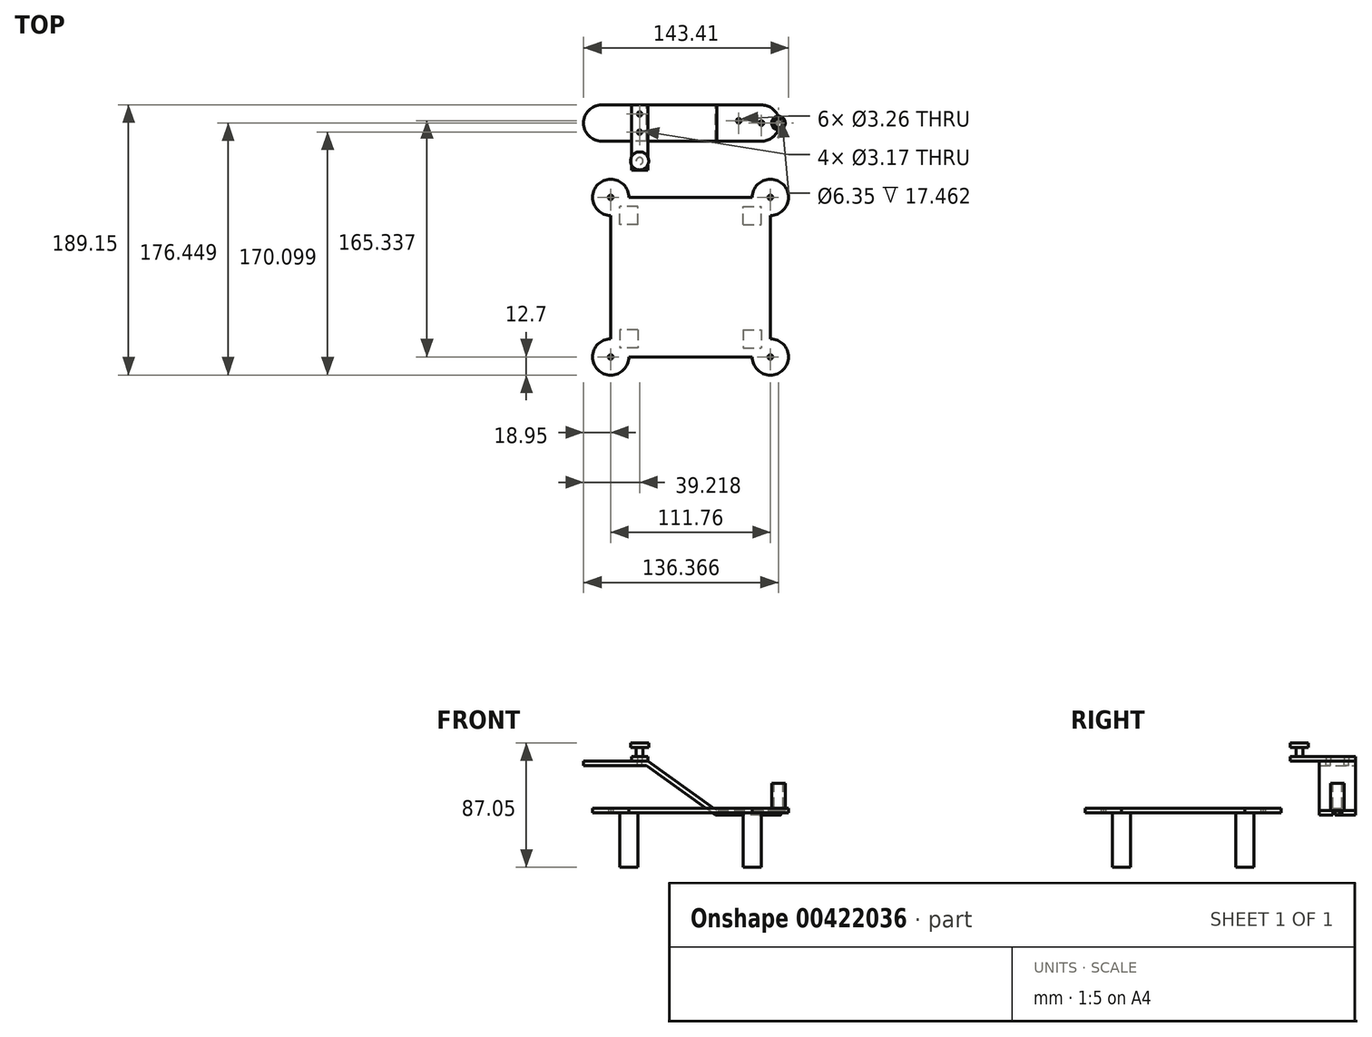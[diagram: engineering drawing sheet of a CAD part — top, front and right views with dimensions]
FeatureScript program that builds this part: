
annotation { "Feature Type Name" : "Feature", "Feature Type Description" : "" }
export const myFeature = defineFeature(function(context is Context, id is Id, definition is map)
    precondition{}
    {
        {
            var Q0;
            Q0=qCreatedBy(makeId("Top.planeOp"),FACE);
            var sketch = newSketch(context, id + "F0", { "sketchPlane" : qUnion([Q0])});
            skLineSegment(sketch, "E0.bottom", {"start": v(-43.18, 55.88) * mm, "end": v(43.18, 55.88) * mm});
            skLineSegment(sketch, "E0.top", {"start": v(-43.18, -55.88) * mm, "end": v(43.18, -55.88) * mm});
            skLineSegment(sketch, "E0.left", {"start": v(-55.88, 43.18) * mm, "end": v(-55.88, -43.18) * mm});
            skLineSegment(sketch, "E0.right", {"start": v(55.88, 43.18) * mm, "end": v(55.88, -43.18) * mm});
            skPoint(sketch, "E0.middle", {"position": v(0, 0) * mm});
            skArc(sketch, "E1", {"start": v(-43.18, 55.88) * mm, "mid": v(-64.86, 64.86) * mm, "end": v(-55.88, 43.18) * mm});
            skLineSegment(sketch, "E2", {"start": v(0, 0) * mm, "end": v(-55.88, 55.88) * mm, "construction": true});
            skArc(sketch, "E3.1.0", {"start": v(-55.88, -43.18) * mm, "mid": v(-64.86, -64.86) * mm, "end": v(-43.18, -55.88) * mm});
            skArc(sketch, "E3.2.0", {"start": v(43.18, -55.88) * mm, "mid": v(64.86, -64.86) * mm, "end": v(55.88, -43.18) * mm});
            skArc(sketch, "E3.3.0", {"start": v(55.88, 43.18) * mm, "mid": v(64.86, 64.86) * mm, "end": v(43.18, 55.88) * mm});
            skLineSegment(sketch, "E4.bottom", {"start": v(31.75, 31.75) * mm, "end": v(-31.75, 31.75) * mm, "construction": true});
            skLineSegment(sketch, "E4.top", {"start": v(31.75, -31.75) * mm, "end": v(-31.75, -31.75) * mm, "construction": true});
            skLineSegment(sketch, "E4.left", {"start": v(31.75, 31.75) * mm, "end": v(31.75, -31.75) * mm, "construction": true});
            skLineSegment(sketch, "E4.right", {"start": v(-31.75, 31.75) * mm, "end": v(-31.75, -31.75) * mm, "construction": true});
            skLineSegment(sketch, "E5.bottom", {"start": v(-43.18, 55.88) * mm, "end": v(39.63, 55.88) * mm});
            skLineSegment(sketch, "E5.top", {"start": v(-43.18, 43.18) * mm, "end": v(39.63, 43.18) * mm});
            skLineSegment(sketch, "E5.left", {"start": v(-43.18, 55.88) * mm, "end": v(-43.18, 43.18) * mm});
            skLineSegment(sketch, "E5.right", {"start": v(39.63, 55.88) * mm, "end": v(39.63, 43.18) * mm});
            skLineSegment(sketch, "E6", {"start": v(14.97, 68.58) * mm, "end": v(-33.08, 68.58) * mm, "construction": true});
            skLineSegment(sketch, "E7", {"start": v(0, 29.37) * mm, "end": v(-29.37, 29.37) * mm, "construction": true});
            skLineSegment(sketch, "E8", {"start": v(-29.37, -8.95) * mm, "end": v(-29.37, 29.37) * mm, "construction": true});
            skSolve(sketch);
        }
        {
            var Q0;
            Q0=qCreatedBy(makeId("Top.planeOp"),FACE);
            var sketch = newSketch(context, id + "F1", { "sketchPlane" : qUnion([Q0])});
            skArc(sketch, "E9", {"start": v(-62.13, 120.57) * mm, "mid": v(-74.83, 107.87) * mm, "end": v(-62.13, 95.17) * mm});
            skLineSegment(sketch, "E10.bottom", {"start": v(-62.13, 95.17) * mm, "end": v(-62.13, 120.57) * mm, "construction": true});
            skLineSegment(sketch, "E10.top", {"start": v(49.63, 95.17) * mm, "end": v(49.63, 120.57) * mm, "construction": true});
            skLineSegment(sketch, "E10.left", {"start": v(-62.13, 95.17) * mm, "end": v(49.63, 95.17) * mm});
            skLineSegment(sketch, "E10.right", {"start": v(-62.13, 120.57) * mm, "end": v(49.63, 120.57) * mm});
            skPoint(sketch, "E10.middle", {"position": v(-6.25, 107.87) * mm});
            skArc(sketch, "E11", {"start": v(49.63, 95.17) * mm, "mid": v(62.33, 107.87) * mm, "end": v(49.63, 120.57) * mm});
            skArc(sketch, "E12", {"start": v(-62.13, 95.17) * mm, "mid": v(-49.43, 107.87) * mm, "end": v(-62.13, 120.57) * mm, "construction": true});
            skCircle(sketch, "E13", {"center": v(49.63, 107.87) * mm, "radius": 12.7 * mm, "construction": true});
            skLineSegment(sketch, "E14", {"start": v(49.63, 107.87) * mm, "end": v(-62.13, 107.87) * mm, "construction": true});
            skPoint(sketch, "E15", {"position": v(36.93, 107.87) * mm});
            skPoint(sketch, "E16", {"position": v(-49.43, 107.87) * mm});
            skSolve(sketch);
        }
        {
            var Q0;
            Q0 = qSketchRegion(id + "F0", true);
            extrude(context, id + "F2", {"entities" : qUnion([Q0]), "depth" : 3.17 * mm});
        }
        {
            var Q0;
            Q0=sQuery(id+"F0.wireOp",VERTEX,"E2.end");
            var Q1;
            Q1=sQuery(id+"F0.wireOp",VERTEX,"E3.3.0.center");
            var Q2;
            Q2=sQuery(id+"F0.wireOp",VERTEX,"E3.1.0.center");
            var Q3;
            Q3=sQuery(id+"F0.wireOp",VERTEX,"E3.2.0.center");
            var Q4;
            Q4=makeQuery(id+"F2.opExtrude","SWEPT_BODY",BODY,{"disambiguationData":[OSD([sQuery(id+"F0.wireOp",EDGE,"E0.bottom"),sQuery(id+"F0.wireOp",EDGE,"E0.top"),sQuery(id+"F0.wireOp",EDGE,"E0.left"),sQuery(id+"F0.wireOp",EDGE,"E0.right"),sQuery(id+"F0.wireOp",EDGE,"E1"),sQuery(id+"F0.wireOp",EDGE,"E3.1.0"),sQuery(id+"F0.wireOp",EDGE,"E3.2.0"),sQuery(id+"F0.wireOp",EDGE,"E3.3.0")])]});
            hole(context, id + "F3", {"style" : HoleStyle.SIMPLE, "endStyle" : HoleEndStyle.THROUGH, "oppositeDirection" : true, "standardTappedOrClearance" : lookupTablePath({ "standard" : "ANSI", "fit" : "Normal (ASME)", "size" : "#4", "type" : "Clearance" }), "standardBlindInLast" : lookupTablePath({ "fit" : "Free", "standard" : "ANSI", "size" : "#4", "type" : "Clearance" }), "holeDiameter" : 3.26 * mm, "isTappedThrough" : true, "tappedDepth" : 12.7 * mm, "tapClearance" : 3, "locations" : qUnion([Q0, Q1, Q2, Q3]), "scope" : qUnion([Q4])});
        }
        {
            var Q0;
            Q0=sQuery(id+"F1.wireOp",EDGE,"E14");
            cPlane(context, id + "F4", {"entities" : qUnion([Q0]), "cplaneType" : CPlaneType.LINE_ANGLE, "offset" : 25.4 * mm, "angle" : 0 * degree, "width" : 152.4 * mm, "height" : 152.4 * mm});
        }
        {
            var Q0;
            Q0=qCreatedBy(id+"F4.planeOp",FACE);
            var sketch = newSketch(context, id + "F5", { "sketchPlane" : qUnion([Q0])});
            skLineSegment(sketch, "E17", {"start": v(49.63, 0) * mm, "end": v(17.88, 0) * mm});
            skLineSegment(sketch, "E18", {"start": v(17.88, 0) * mm, "end": v(-30.38, 34.66) * mm});
            skLineSegment(sketch, "E19", {"start": v(-30.38, 34.66) * mm, "end": v(-62.13, 34.66) * mm});
            skLineSegment(sketch, "E20", {"start": v(-30.38, 34.66) * mm, "end": v(-30.38, 0.01) * mm, "construction": true});
            skLineSegment(sketch, "E21", {"start": v(-62.13, 34.66) * mm, "end": v(-62.13, 0) * mm, "construction": true});
            skSolve(sketch);
        }
        {
            var Q0;
            Q0=sQuery(id+"F1.wireOp",EDGE,"E10.top");
            cPlane(context, id + "F6", {"entities" : qUnion([Q0]), "cplaneType" : CPlaneType.LINE_ANGLE, "offset" : 25.4 * mm, "angle" : 90 * degree, "width" : 152.4 * mm, "height" : 152.4 * mm});
        }
        {
            var Q0;
            Q0=qCreatedBy(id+"F6.planeOp",FACE);
            var sketch = newSketch(context, id + "F7", { "sketchPlane" : qUnion([Q0])});
            skLineSegment(sketch, "E22.bottom", {"start": v(95.17, -1.59) * mm, "end": v(120.57, -1.59) * mm});
            skLineSegment(sketch, "E22.top", {"start": v(95.17, 1.59) * mm, "end": v(120.57, 1.59) * mm});
            skLineSegment(sketch, "E22.left", {"start": v(95.17, -1.59) * mm, "end": v(95.17, 1.59) * mm});
            skLineSegment(sketch, "E22.right", {"start": v(120.57, -1.59) * mm, "end": v(120.57, 1.59) * mm});
            skPoint(sketch, "E23", {"position": v(120.57, 0) * mm});
            skSolve(sketch);
        }
        {
            var Q0;
            Q0 = qSketchRegion(id + "F7", true);
            var Q1;
            Q1 = qConstructionFilter(qBodyType(qCreatedBy(id + "F5" ,EDGE), BodyType.WIRE), ConstructionObject.NO);
            sweep(context, id + "F8", {"profiles" : qUnion([Q0]), "path" : qUnion([Q1])});
        }
        {
            var Q0;
            Q0=makeQuery(id+"F8.opSweep","CAP_FACE",FACE,{"disambiguationData":[OSD([sQuery(id+"F5.wireOp",VERTEX,"E17.start"),sQuery(id+"F7.wireOp",EDGE,"E22.bottom"),sQuery(id+"F7.wireOp",EDGE,"E22.top"),sQuery(id+"F7.wireOp",EDGE,"E22.left"),sQuery(id+"F7.wireOp",EDGE,"E22.right")])],"isStart":true});
            var sketch = newSketch(context, id + "F9", { "sketchPlane" : qUnion([Q0])});
            skLineSegment(sketch, "E24", {"start": v(107.87, 1.59) * mm, "end": v(107.87, -1.59) * mm, "construction": true});
            skLineSegment(sketch, "E25.bottom", {"start": v(107.87, 1.59) * mm, "end": v(120.57, 1.59) * mm});
            skLineSegment(sketch, "E25.top", {"start": v(107.87, -1.59) * mm, "end": v(120.57, -1.59) * mm});
            skLineSegment(sketch, "E25.left", {"start": v(107.87, 1.59) * mm, "end": v(107.87, -1.59) * mm});
            skLineSegment(sketch, "E25.right", {"start": v(120.57, 1.59) * mm, "end": v(120.57, -1.59) * mm});
            skSolve(sketch);
        }
        {
            var Q0;
            Q0 = qSketchRegion(id + "F9", true);
            var Q1;
            Q1=sQuery(id+"F9.wireOp",EDGE,"E25.left");
            revolve(context, id + "F10", {"operationType" : NewBodyOperationType.ADD, "entities" : qUnion([Q0]), "axis" : qUnion([Q1]), "revolveType" : RevolveType.FULL});
        }
        {
            var Q0;
            Q0=makeQuery(id+"F8.opSweep","CAP_FACE",FACE,{"disambiguationData":[OSD([sQuery(id+"F5.wireOp",VERTEX,"E19.end"),sQuery(id+"F7.wireOp",EDGE,"E22.bottom"),sQuery(id+"F7.wireOp",EDGE,"E22.top"),sQuery(id+"F7.wireOp",EDGE,"E22.left"),sQuery(id+"F7.wireOp",EDGE,"E22.right")])],"isStart":false});
            var sketch = newSketch(context, id + "F11", { "sketchPlane" : qUnion([Q0])});
            skLineSegment(sketch, "E26", {"start": v(-107.87, 36.25) * mm, "end": v(-107.87, 33.07) * mm, "construction": true});
            skLineSegment(sketch, "E27.bottom", {"start": v(-107.87, 33.07) * mm, "end": v(-95.17, 33.07) * mm});
            skLineSegment(sketch, "E27.top", {"start": v(-107.87, 36.25) * mm, "end": v(-95.17, 36.25) * mm});
            skLineSegment(sketch, "E27.left", {"start": v(-107.87, 33.07) * mm, "end": v(-107.87, 36.25) * mm});
            skLineSegment(sketch, "E27.right", {"start": v(-95.17, 33.07) * mm, "end": v(-95.17, 36.25) * mm});
            skSolve(sketch);
        }
        {
            var Q0;
            Q0 = qSketchRegion(id + "F11", true);
            var Q1;
            Q1=sQuery(id+"F11.wireOp",EDGE,"E27.left");
            revolve(context, id + "F12", {"operationType" : NewBodyOperationType.ADD, "entities" : qUnion([Q0]), "axis" : qUnion([Q1]), "revolveType" : RevolveType.FULL});
        }
        {
            var Q0;
            Q0=makeQuery(id+"F10.boolean.opBoolean","MERGE",FACE,{"derivedFrom":[makeQuery(id+"F8.opSweep","SWEPT_FACE",FACE,{"disambiguationData":[OSD([sQuery(id+"F5.wireOp",EDGE,"E17"),sQuery(id+"F7.wireOp",EDGE,"E22.top")])]}),makeQuery(id+"F10.opRevolve","SWEPT_FACE",FACE,{"disambiguationData":[OSD([sQuery(id+"F9.wireOp",EDGE,"E25.bottom")])]})]});
            var sketch = newSketch(context, id + "F13", { "sketchPlane" : qUnion([Q0])});
            skPoint(sketch, "E28", {"position": v(49.63, 107.87) * mm});
            skSolve(sketch);
        }
        {
            var Q0;
            Q0=sQuery(id+"F13.wireOp",VERTEX,"E28");
            var Q1;
            Q1=makeQuery(id+"F8.opSweep","SWEPT_BODY",BODY,{"disambiguationData":[OSD([sQuery(id+"F5.wireOp",EDGE,"E19"),sQuery(id+"F7.wireOp",EDGE,"E22.bottom"),sQuery(id+"F7.wireOp",EDGE,"E22.top"),sQuery(id+"F7.wireOp",EDGE,"E22.left"),sQuery(id+"F7.wireOp",EDGE,"E22.right")])]});
            hole(context, id + "F14", {"style" : HoleStyle.SIMPLE, "endStyle" : HoleEndStyle.THROUGH, "standardTappedOrClearance" : lookupTablePath({ "standard" : "ANSI", "fit" : "Normal (ASME)", "size" : "#4", "type" : "Clearance" }), "standardBlindInLast" : lookupTablePath({ "fit" : "Free", "standard" : "ANSI", "size" : "#4", "type" : "Clearance" }), "holeDiameter" : 3.26 * mm, "isTappedThrough" : true, "tappedDepth" : 12.7 * mm, "tapClearance" : 3, "locations" : qUnion([Q0]), "scope" : qUnion([Q1])});
        }
        {
            var Q0;
            Q0=makeQuery(id+"F10.boolean.opBoolean","MERGE",FACE,{"derivedFrom":[makeQuery(id+"F8.opSweep","SWEPT_FACE",FACE,{"disambiguationData":[OSD([sQuery(id+"F5.wireOp",EDGE,"E17"),sQuery(id+"F7.wireOp",EDGE,"E22.top")])]}),makeQuery(id+"F10.opRevolve","SWEPT_FACE",FACE,{"disambiguationData":[OSD([sQuery(id+"F9.wireOp",EDGE,"E25.bottom")])]})]});
            var sketch = newSketch(context, id + "F15", { "sketchPlane" : qUnion([Q0])});
            skPoint(sketch, "E29", {"position": v(33.76, 109.46) * mm});
            skSolve(sketch);
        }
        {
            var Q0;
            Q0=sQuery(id+"F15.wireOp",VERTEX,"E29");
            var Q1;
            Q1=makeQuery(id+"F8.opSweep","SWEPT_BODY",BODY,{"disambiguationData":[OSD([sQuery(id+"F5.wireOp",EDGE,"E19"),sQuery(id+"F7.wireOp",EDGE,"E22.bottom"),sQuery(id+"F7.wireOp",EDGE,"E22.top"),sQuery(id+"F7.wireOp",EDGE,"E22.left"),sQuery(id+"F7.wireOp",EDGE,"E22.right")])]});
            hole(context, id + "F16", {"style" : HoleStyle.SIMPLE, "endStyle" : HoleEndStyle.THROUGH, "standardTappedOrClearance" : lookupTablePath({ "standard" : "ANSI", "fit" : "Normal (ASME)", "size" : "#4", "type" : "Clearance" }), "standardBlindInLast" : lookupTablePath({ "fit" : "Free", "standard" : "ANSI", "size" : "#4", "type" : "Clearance" }), "holeDiameter" : 3.26 * mm, "isTappedThrough" : true, "tappedDepth" : 12.7 * mm, "tapClearance" : 3, "locations" : qUnion([Q0]), "scope" : qUnion([Q1])});
        }
        {
            var Q0;
            Q0=makeQuery(id+"F10.boolean.opBoolean","MERGE",FACE,{"derivedFrom":[makeQuery(id+"F8.opSweep","SWEPT_FACE",FACE,{"disambiguationData":[OSD([sQuery(id+"F5.wireOp",EDGE,"E17"),sQuery(id+"F7.wireOp",EDGE,"E22.top")])]}),makeQuery(id+"F10.opRevolve","SWEPT_FACE",FACE,{"disambiguationData":[OSD([sQuery(id+"F9.wireOp",EDGE,"E25.bottom")])]})]});
            var sketch = newSketch(context, id + "F17", { "sketchPlane" : qUnion([Q0])});
            skPoint(sketch, "E30", {"position": v(62.33, 107.87) * mm});
            skCircle(sketch, "E31", {"center": v(62.33, 107.87) * mm, "radius": 1.59 * mm, "construction": true});
            skCircle(sketch, "E32", {"center": v(62.33, 107.87) * mm, "radius": 3.18 * mm, "construction": true});
            skLineSegment(sketch, "E33.bottom", {"start": v(65.5, 111.04) * mm, "end": v(59.16, 111.04) * mm});
            skLineSegment(sketch, "E33.top", {"start": v(65.5, 104.7) * mm, "end": v(59.16, 104.7) * mm});
            skLineSegment(sketch, "E33.left", {"start": v(65.5, 111.04) * mm, "end": v(65.5, 104.7) * mm});
            skLineSegment(sketch, "E33.right", {"start": v(59.16, 111.04) * mm, "end": v(59.16, 104.7) * mm});
            skSolve(sketch);
        }
        {
            var Q0;
            Q0 = qSketchRegion(id + "F17", true);
            extrude(context, id + "F18", {"entities" : qUnion([Q0]), "operationType" : NewBodyOperationType.REMOVE, "endBound" : BoundingType.THROUGH_ALL, "oppositeDirection" : true, "depth" : 25.4 * mm});
        }
        {
            var Q0;
            Q0=makeQuery(id+"F10.boolean.opBoolean","MERGE",FACE,{"derivedFrom":[makeQuery(id+"F8.opSweep","SWEPT_FACE",FACE,{"disambiguationData":[OSD([sQuery(id+"F5.wireOp",EDGE,"E17"),sQuery(id+"F7.wireOp",EDGE,"E22.top")])]}),makeQuery(id+"F10.opRevolve","SWEPT_FACE",FACE,{"disambiguationData":[OSD([sQuery(id+"F9.wireOp",EDGE,"E25.bottom")])]})]});
            var sketch = newSketch(context, id + "F19", { "sketchPlane" : qUnion([Q0])});
            skCircle(sketch, "E34", {"center": v(61.54, 107.87) * mm, "radius": 1.59 * mm});
            skPoint(sketch, "E34.centerSnap0", {"position": v(59.16, 107.87) * mm});
            skSolve(sketch);
        }
        {
            var Q0;
            Q0 = qSketchRegion(id + "F19", true);
            extrude(context, id + "F20", {"entities" : qUnion([Q0]), "oppositeDirection" : true, "depth" : 3.17 * mm});
        }
        {
            var Q0;
            Q0=makeQuery(id+"F20.opExtrude","CAP_FACE",FACE,{"disambiguationData":[OSD([sQuery(id+"F19.wireOp",EDGE,"E34")])],"isStart":true});
            var sketch = newSketch(context, id + "F21", { "sketchPlane" : qUnion([Q0])});
            skCircle(sketch, "E35", {"center": v(61.54, 107.87) * mm, "radius": 4.76 * mm});
            skSolve(sketch);
        }
        {
            var Q0;
            Q0 = qSketchRegion(id + "F21", true);
            extrude(context, id + "F22", {"entities" : qUnion([Q0]), "operationType" : NewBodyOperationType.ADD, "depth" : 19.05 * mm});
        }
        {
            var Q0;
            Q0=makeQuery(id+"F22.opExtrude","CAP_FACE",FACE,{"disambiguationData":[OSD([sQuery(id+"F21.wireOp",EDGE,"E35")])],"isStart":false});
            var sketch = newSketch(context, id + "F23", { "sketchPlane" : qUnion([Q0])});
            skCircle(sketch, "E36", {"center": v(61.54, 107.87) * mm, "radius": 3.18 * mm});
            skSolve(sketch);
        }
        {
            var Q0;
            Q0 = qSketchRegion(id + "F23", true);
            extrude(context, id + "F24", {"entities" : qUnion([Q0]), "operationType" : NewBodyOperationType.REMOVE, "oppositeDirection" : true, "depth" : 17.46 * mm});
        }
        {
            var Q0;
            Q0=makeQuery(id+"F12.boolean.opBoolean","MERGE",FACE,{"derivedFrom":[makeQuery(id+"F8.opSweep","SWEPT_FACE",FACE,{"disambiguationData":[OSD([sQuery(id+"F5.wireOp",EDGE,"E19"),sQuery(id+"F7.wireOp",EDGE,"E22.top")])]}),makeQuery(id+"F12.opRevolve","SWEPT_FACE",FACE,{"disambiguationData":[OSD([sQuery(id+"F11.wireOp",EDGE,"E27.top")])]})]});
            var sketch = newSketch(context, id + "F25", { "sketchPlane" : qUnion([Q0])});
            skPoint(sketch, "E37", {"position": v(-35.61, 107.87) * mm});
            skSolve(sketch);
        }
        {
            var Q0;
            {var subQ0=sQuery(id+"F7.wireOp",EDGE,"E22.top");Q0=makeQuery(id+"F25.imprint","IMPRINT",FACE,{"disambiguationData":[TD([[makeQuery(id+"F25.imprint","IMPRINT",EDGE,{"derivedFrom":makeQuery(id+"F8.opSweep","MID_CAP_EDGE",EDGE,{"disambiguationData":[OSD([sQuery(id+"F5.wireOp",VERTEX,"E19.start"),subQ0])],"capPos":2.0})}),-1.0]])]});}
            var sketch = newSketch(context, id + "F26", { "sketchPlane" : qUnion([Q0])});
            skCircle(sketch, "E38", {"center": v(-35.61, 114.22) * mm, "radius": 1.59 * mm});
            skCircle(sketch, "E39", {"center": v(-35.61, 101.52) * mm, "radius": 1.59 * mm});
            skLineSegment(sketch, "E40", {"start": v(-35.61, 114.22) * mm, "end": v(-35.61, 101.52) * mm, "construction": true});
            skSolve(sketch);
        }
        {
            var Q0;
            Q0 = qSketchRegion(id + "F26", true);
            extrude(context, id + "F27", {"entities" : qUnion([Q0]), "operationType" : NewBodyOperationType.REMOVE, "oppositeDirection" : true, "depth" : 25.4 * mm});
        }
        {
            var Q0;
            {var subQ0=sQuery(id+"F7.wireOp",EDGE,"E22.top");Q0=makeQuery(id+"F25.imprint","IMPRINT",FACE,{"disambiguationData":[TD([[makeQuery(id+"F25.imprint","IMPRINT",EDGE,{"derivedFrom":makeQuery(id+"F8.opSweep","MID_CAP_EDGE",EDGE,{"disambiguationData":[OSD([sQuery(id+"F5.wireOp",VERTEX,"E19.start"),subQ0])],"capPos":2.0})}),-1.0]])]});}
            var sketch = newSketch(context, id + "F28", { "sketchPlane" : qUnion([Q0])});
            skLineSegment(sketch, "E41.bottom", {"start": v(-41.36, 120.57) * mm, "end": v(-29.87, 120.57) * mm});
            skLineSegment(sketch, "E41.top", {"start": v(-41.36, 75) * mm, "end": v(-29.87, 75) * mm});
            skLineSegment(sketch, "E41.left", {"start": v(-41.36, 120.57) * mm, "end": v(-41.36, 75) * mm});
            skLineSegment(sketch, "E41.right", {"start": v(-29.87, 120.57) * mm, "end": v(-29.87, 75) * mm});
            skCircle(sketch, "E42", {"center": v(-35.61, 81.35) * mm, "radius": 2.38 * mm, "construction": true});
            skLineSegment(sketch, "E43", {"start": v(-35.61, 120.57) * mm, "end": v(-35.61, 75) * mm, "construction": true});
            skPoint(sketch, "E44", {"position": v(-35.61, 107.87) * mm});
            skCircle(sketch, "E45.0", {"center": v(-35.61, 101.52) * mm, "radius": 1.59 * mm});
            skCircle(sketch, "E46.0", {"center": v(-35.61, 114.22) * mm, "radius": 1.59 * mm});
            skSolve(sketch);
        }
        {
            var Q0;
            Q0 = qSketchRegion(id + "F28", true);
            extrude(context, id + "F29", {"entities" : qUnion([Q0]), "depth" : 3.17 * mm});
        }
        {
            var Q0;
            Q0=makeQuery(id+"F29.opExtrude","CAP_FACE",FACE,{"disambiguationData":[OSD([sQuery(id+"F28.wireOp",EDGE,"E41.bottom"),sQuery(id+"F28.wireOp",EDGE,"E41.top"),sQuery(id+"F28.wireOp",EDGE,"E41.left"),sQuery(id+"F28.wireOp",EDGE,"E41.right"),sQuery(id+"F28.wireOp",EDGE,"E45.0"),sQuery(id+"F28.wireOp",EDGE,"E46.0")])],"isStart":false});
            var sketch = newSketch(context, id + "F30", { "sketchPlane" : qUnion([Q0])});
            skCircle(sketch, "E47.0", {"center": v(-35.61, 81.35) * mm, "radius": 2.38 * mm});
            skSolve(sketch);
        }
        {
            var Q0;
            Q0 = qSketchRegion(id + "F30", true);
            extrude(context, id + "F31", {"entities" : qUnion([Q0]), "operationType" : NewBodyOperationType.ADD, "depth" : 6.35 * mm});
        }
        {
            var Q0;
            Q0=makeQuery(id+"F31.opExtrude","CAP_FACE",FACE,{"disambiguationData":[OSD([sQuery(id+"F30.wireOp",EDGE,"E47.0")])],"isStart":false});
            var sketch = newSketch(context, id + "F32", { "sketchPlane" : qUnion([Q0])});
            skCircle(sketch, "E48", {"center": v(-35.61, 81.35) * mm, "radius": 6.35 * mm});
            skSolve(sketch);
        }
        {
            var Q0;
            Q0 = qSketchRegion(id + "F32", true);
            extrude(context, id + "F33", {"entities" : qUnion([Q0]), "operationType" : NewBodyOperationType.ADD, "depth" : 3.17 * mm});
        }
        {
            var Q0;
            Q0=makeQuery(id+"F0.imprint","IMPRINT",FACE,{"disambiguationData":[TD([[makeQuery(id+"F0.imprint","IMPRINT",EDGE,{"derivedFrom":sQuery(id+"F0.wireOp",EDGE,"E0.bottom")}),-1.0]])]});
            var sketch = newSketch(context, id + "F34", { "sketchPlane" : qUnion([Q0])});
            skLineSegment(sketch, "E49.bottom", {"start": v(-36.83, -36.83) * mm, "end": v(-49.53, -36.83) * mm});
            skLineSegment(sketch, "E49.top", {"start": v(-36.83, -49.53) * mm, "end": v(-49.53, -49.53) * mm});
            skLineSegment(sketch, "E49.left", {"start": v(-36.83, -36.83) * mm, "end": v(-36.83, -49.53) * mm});
            skLineSegment(sketch, "E49.right", {"start": v(-49.53, -36.83) * mm, "end": v(-49.53, -49.53) * mm});
            skPoint(sketch, "E49.middle", {"position": v(-43.18, -43.18) * mm});
            skLineSegment(sketch, "E50.1.0", {"start": v(36.83, -36.83) * mm, "end": v(49.53, -36.83) * mm});
            skLineSegment(sketch, "E50.1.1", {"start": v(36.83, -49.53) * mm, "end": v(49.53, -49.53) * mm});
            skLineSegment(sketch, "E50.1.2", {"start": v(36.83, -36.83) * mm, "end": v(36.83, -49.53) * mm});
            skLineSegment(sketch, "E50.1.3", {"start": v(49.53, -36.83) * mm, "end": v(49.53, -49.53) * mm});
            skPoint(sketch, "E50.1.4", {"position": v(43.18, -43.18) * mm});
            skLineSegment(sketch, "E50.2.0", {"start": v(36.83, 36.83) * mm, "end": v(36.83, 49.53) * mm});
            skLineSegment(sketch, "E50.2.1", {"start": v(49.53, 36.83) * mm, "end": v(49.53, 49.53) * mm});
            skLineSegment(sketch, "E50.2.2", {"start": v(36.83, 36.83) * mm, "end": v(49.53, 36.83) * mm});
            skLineSegment(sketch, "E50.2.3", {"start": v(36.83, 49.53) * mm, "end": v(49.53, 49.53) * mm});
            skPoint(sketch, "E50.2.4", {"position": v(43.18, 43.18) * mm});
            skLineSegment(sketch, "E50.3.0", {"start": v(-36.83, 36.83) * mm, "end": v(-49.53, 36.83) * mm});
            skLineSegment(sketch, "E50.3.1", {"start": v(-36.83, 49.53) * mm, "end": v(-49.53, 49.53) * mm});
            skLineSegment(sketch, "E50.3.2", {"start": v(-36.83, 36.83) * mm, "end": v(-36.83, 49.53) * mm});
            skLineSegment(sketch, "E50.3.3", {"start": v(-49.53, 36.83) * mm, "end": v(-49.53, 49.53) * mm});
            skPoint(sketch, "E50.3.4", {"position": v(-43.18, 43.18) * mm});
            skPoint(sketch, "E50.center", {"position": v(0, 0) * mm});
            skSolve(sketch);
        }
        {
            var Q0;
            Q0 = qSketchRegion(id + "F34", true);
            extrude(context, id + "F35", {"entities" : qUnion([Q0]), "operationType" : NewBodyOperationType.ADD, "oppositeDirection" : true, "depth" : 38.1 * mm});
        }
    });
